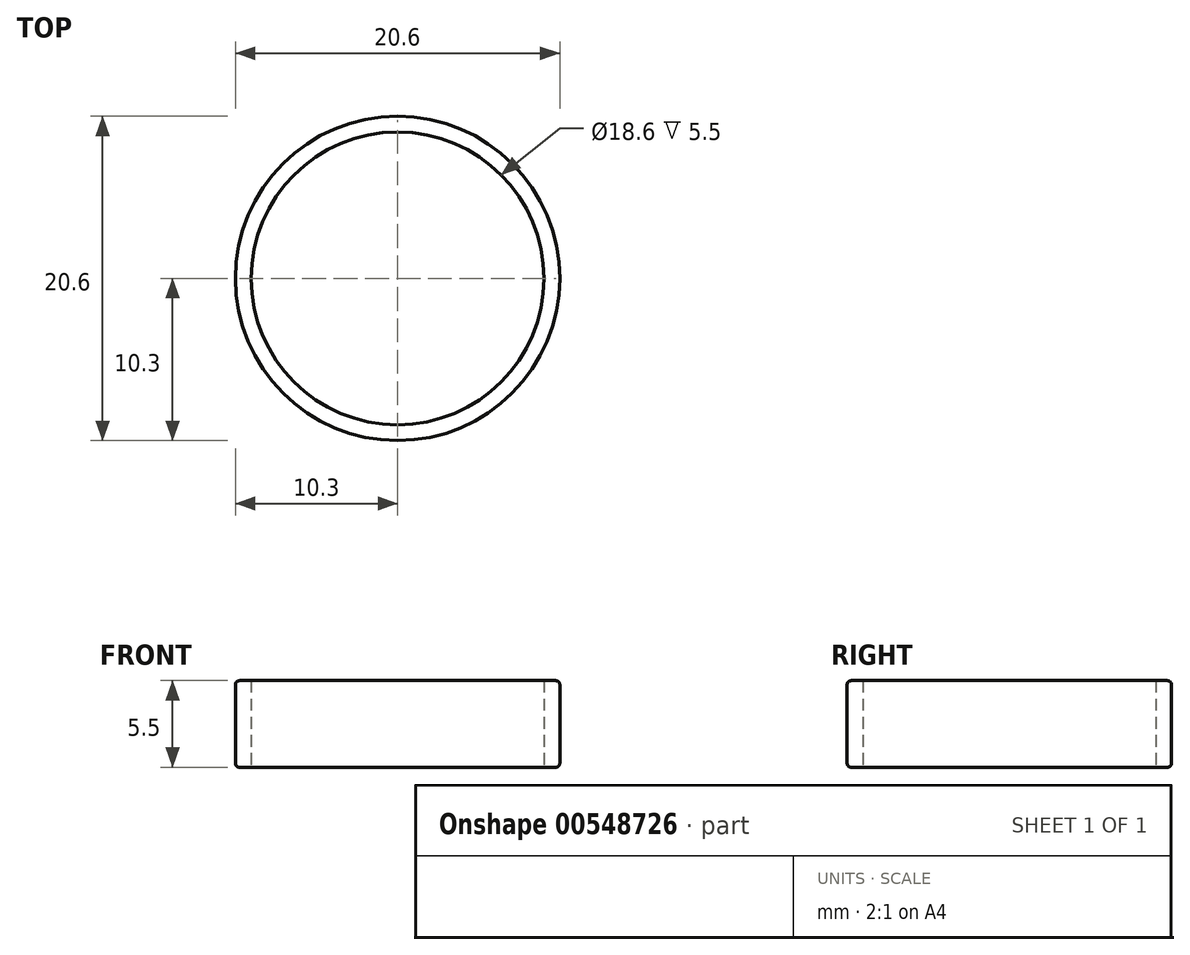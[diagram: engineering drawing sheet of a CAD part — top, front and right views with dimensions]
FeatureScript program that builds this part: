
annotation { "Feature Type Name" : "Feature", "Feature Type Description" : "" }
export const myFeature = defineFeature(function(context is Context, id is Id, definition is map)
    precondition{}
    {
        {
            var Q0;
            Q0=qCreatedBy(makeId("Top.planeOp"),FACE);
            var sketch = newSketch(context, id + "F0", { "sketchPlane" : qUnion([Q0])});
            skCircle(sketch, "E0", {"center": v(0, 0) * mm, "radius": 9.3 * mm});
            skCircle(sketch, "E1", {"center": v(0, 0) * mm, "radius": 10.3 * mm});
            skSolve(sketch);
        }
        {
            var Q0;
            Q0=qSketchRegion(id+"F0",true);
            extrude(context, id + "F1", {"entities" : qUnion([Q0]), "depth" : 5.5 * mm, "offsetDistance" : 25 * mm});
        }
        {
            var Q0;
            Q0=makeQuery(id+"F1.opExtrude","CAP_EDGE",EDGE,{"disambiguationData":[OSD([sQuery(id+"F0.wireOp",EDGE,"E1")])],"isStart":true});
            var Q1;
            Q1=makeQuery(id+"F1.opExtrude","CAP_EDGE",EDGE,{"disambiguationData":[OSD([sQuery(id+"F0.wireOp",EDGE,"E1")])],"isStart":false});
            fillet(context, id + "F2", {"entities" : qUnion([Q0, Q1]), "radius" : .25 * mm, "tangentPropagation" : true, "allowEdgeOverflow" : false});
        }
    });
